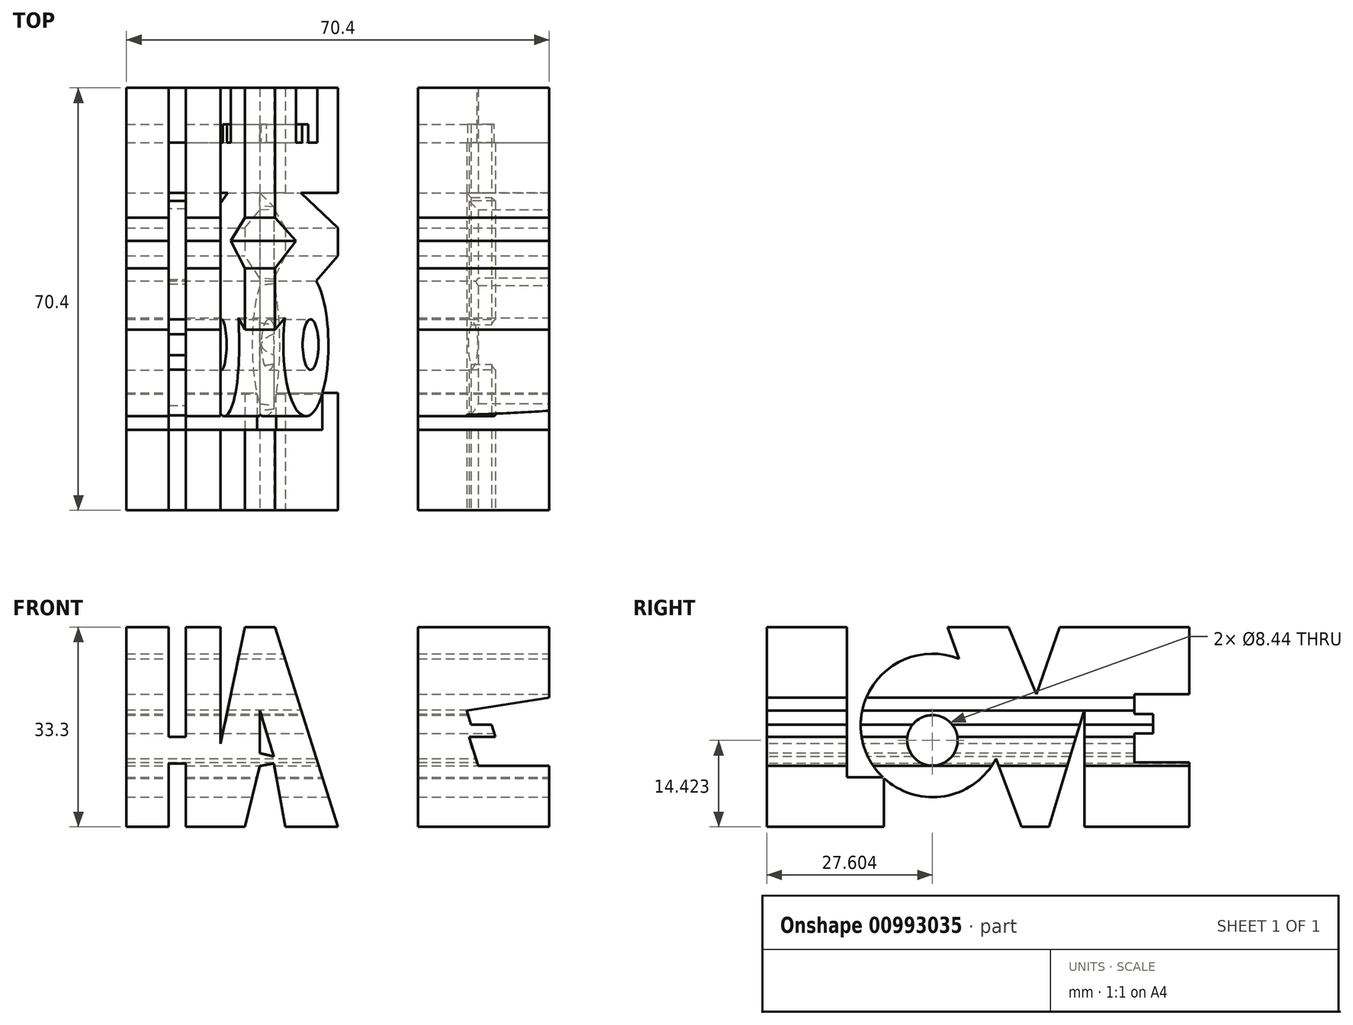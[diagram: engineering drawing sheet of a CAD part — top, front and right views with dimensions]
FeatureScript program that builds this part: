
annotation { "Feature Type Name" : "Feature", "Feature Type Description" : "" }
export const myFeature = defineFeature(function(context is Context, id is Id, definition is map)
    precondition{}
    {
        {
            var Q0;
            Q0=qCreatedBy(makeId("Top.planeOp"),FACE);
            var sketch = newSketch(context, id + "F0", { "sketchPlane" : qUnion([Q0])});
            skLineSegment(sketch, "E0.bottom", {"start": v(35.2, 35.2) * mm, "end": v(-35.2, 35.2) * mm});
            skLineSegment(sketch, "E0.top", {"start": v(35.2, -35.2) * mm, "end": v(-35.2, -35.2) * mm});
            skLineSegment(sketch, "E0.left", {"start": v(35.2, 35.2) * mm, "end": v(35.2, -35.2) * mm});
            skLineSegment(sketch, "E0.right", {"start": v(-35.2, 35.2) * mm, "end": v(-35.2, -35.2) * mm});
            skPoint(sketch, "E0.middle", {"position": v(0, 0) * mm});
            skSolve(sketch);
        }
        {
            var Q0;
            Q0=makeQuery(id+"F0.imprint","IMPRINT",FACE,{"disambiguationData":[TD([[makeQuery(id+"F0.imprint","IMPRINT",EDGE,{"derivedFrom":sQuery(id+"F0.wireOp",EDGE,"E0.bottom")}),1.0]])]});
            extrude(context, id + "F1", {"entities" : qUnion([Q0]), "depth" : 33.3 * mm, "offsetDistance" : 25 * mm});
        }
        {
            var Q0;
            Q0=makeQuery(id+"F1.opExtrude","SWEPT_FACE",FACE,{"disambiguationData":[OSD([sQuery(id+"F0.wireOp",EDGE,"E0.left")])]});
            var sketch = newSketch(context, id + "F2", { "sketchPlane" : qUnion([Q0])});
            skLineSegment(sketch, "E1", {"start": v(-35.2, 33.3) * mm, "end": v(-35.2, 0) * mm});
            skLineSegment(sketch, "E2", {"start": v(-35.2, 0) * mm, "end": v(-15.67, 0) * mm});
            skLineSegment(sketch, "E3", {"start": v(-15.67, 0) * mm, "end": v(-15.67, 8.27) * mm});
            skLineSegment(sketch, "E4", {"start": v(-15.67, 8.27) * mm, "end": v(-21.83, 8.27) * mm});
            skLineSegment(sketch, "E5", {"start": v(-21.83, 8.27) * mm, "end": v(-21.83, 33.3) * mm});
            skLineSegment(sketch, "E6", {"start": v(-21.83, 33.3) * mm, "end": v(-35.2, 33.3) * mm});
            skCircle(sketch, "E7", {"center": v(-7.6, 14.42) * mm, "radius": 4.22 * mm});
            skCircle(sketch, "E8", {"center": v(-7.6, 16.92) * mm, "radius": 11.96 * mm});
            skLineSegment(sketch, "E9", {"start": v(-5.1, 33.3) * mm, "end": v(7.21, 0) * mm});
            skLineSegment(sketch, "E10", {"start": v(7.21, 0) * mm, "end": v(11.83, 0) * mm});
            skLineSegment(sketch, "E11", {"start": v(11.83, 0) * mm, "end": v(21.83, 33.3) * mm});
            skLineSegment(sketch, "E12", {"start": v(21.83, 33.3) * mm, "end": v(13.56, 33.3) * mm});
            skLineSegment(sketch, "E13", {"start": v(13.56, 33.3) * mm, "end": v(9.71, 22.12) * mm});
            skLineSegment(sketch, "E14", {"start": v(9.71, 22.12) * mm, "end": v(5.1, 33.3) * mm});
            skLineSegment(sketch, "E15", {"start": v(5.1, 33.3) * mm, "end": v(-5.1, 33.3) * mm});
            skLineSegment(sketch, "E16", {"start": v(17.7, 33.3) * mm, "end": v(17.7, 0) * mm});
            skLineSegment(sketch, "E17", {"start": v(17.7, 0) * mm, "end": v(35.2, 0) * mm});
            skLineSegment(sketch, "E18", {"start": v(35.2, 0) * mm, "end": v(35.2, 10.77) * mm});
            skLineSegment(sketch, "E19", {"start": v(35.2, 10.77) * mm, "end": v(26.06, 10.77) * mm});
            skLineSegment(sketch, "E20", {"start": v(26.06, 10.77) * mm, "end": v(26.06, 15.58) * mm});
            skLineSegment(sketch, "E21", {"start": v(17.7, 33.3) * mm, "end": v(35.2, 33.3) * mm});
            skLineSegment(sketch, "E22", {"start": v(35.2, 33.3) * mm, "end": v(35.2, 22.12) * mm});
            skLineSegment(sketch, "E23", {"start": v(35.2, 22.12) * mm, "end": v(26.06, 22.12) * mm});
            skLineSegment(sketch, "E24", {"start": v(26.06, 22.12) * mm, "end": v(26.06, 18.85) * mm});
            skLineSegment(sketch, "E25", {"start": v(26.06, 18.85) * mm, "end": v(29.13, 18.85) * mm});
            skLineSegment(sketch, "E26", {"start": v(29.13, 18.85) * mm, "end": v(29.13, 15.58) * mm});
            skLineSegment(sketch, "E27", {"start": v(29.13, 15.58) * mm, "end": v(26.06, 15.58) * mm});
            skSolve(sketch);
        }
        {
            var Q0;
            Q0=makeQuery(id+"F2.imprint","IMPRINT",FACE,{"disambiguationData":[TD([[makeQuery(id+"F2.imprint","IMPRINT",EDGE,{"derivedFrom":sQuery(id+"F2.wireOp",EDGE,"E1")}),1.0]])]});
            var Q1;
            Q1=makeQuery(id+"F2.imprint","IMPRINT",FACE,{"disambiguationData":[TD([[makeQuery(id+"F2.imprint","IMPRINT",EDGE,{"derivedFrom":sQuery(id+"F2.wireOp",EDGE,"E7")}),-1.0]])]});
            var Q2;
            {var subQ0=sQuery(id+"F2.wireOp",EDGE,"E10");Q2=makeQuery(id+"F2.imprint","IMPRINT",FACE,{"disambiguationData":[TD([[makeQuery(id+"F2.imprint","IMPRINT",EDGE,{"derivedFrom":subQ0}),-1.0]])]});}
            var Q3;
            {var subQ0=sQuery(id+"F2.wireOp",EDGE,"E21");var subQ1=sQuery(id+"F2.wireOp",EDGE,"E11");var subQ2=makeQuery(id+"F2.imprint","INTERSECT",VERTEX,{"derivedFrom":[subQ1,subQ0]});Q3=makeQuery(id+"F2.imprint","IMPRINT",FACE,{"disambiguationData":[TD([[makeQuery(id+"F2.imprint","IMPRINT",EDGE,{"disambiguationData":[TD([[subQ2,1.0]])],"derivedFrom":subQ1}),1.0]])]});}
            var Q4;
            {var subQ6=sQuery(id+"F2.wireOp",EDGE,"E17");Q4=makeQuery(id+"F2.imprint","IMPRINT",FACE,{"disambiguationData":[TD([[makeQuery(id+"F2.imprint","IMPRINT",EDGE,{"derivedFrom":subQ6}),-1.0]])]});}
            var Q5;
            {var subQ0=sQuery(id+"F2.wireOp",EDGE,"E9");var subQ1=sQuery(id+"F2.wireOp",EDGE,"E8");var subQ2=makeQuery(id+"F2.imprint","INTERSECT",VERTEX,{"disambiguationData":[OD(0.0)],"derivedFrom":[subQ1,subQ0]});Q5=makeQuery(id+"F2.imprint","IMPRINT",FACE,{"disambiguationData":[TD([[makeQuery(id+"F2.imprint","IMPRINT",EDGE,{"disambiguationData":[TD([[subQ2,1.0]])],"derivedFrom":subQ1}),1.0]])]});}
            var Q6;
            {var subQ0=sQuery(id+"F2.wireOp",EDGE,"E4");var subQ1=sQuery(id+"F2.wireOp",EDGE,"E3");var subQ2=makeQuery(id+"F2.imprint","INTERSECT",VERTEX,{"derivedFrom":[subQ1,subQ0]});Q6=makeQuery(id+"F2.imprint","IMPRINT",FACE,{"disambiguationData":[TD([[makeQuery(id+"F2.imprint","IMPRINT",EDGE,{"disambiguationData":[TD([[subQ2,1.0]])],"derivedFrom":subQ1}),1.0]])]});}
            extrude(context, id + "F3", {"entities" : qUnion([Q0, Q1, Q2, Q3, Q4, Q5, Q6]), "operationType" : NewBodyOperationType.INTERSECT, "oppositeDirection" : true, "depth" : 88.7 * mm, "offsetDistance" : 25 * mm});
        }
        {
            var Q0;
            Q0=makeQuery(id+"F1.opExtrude","SWEPT_FACE",FACE,{"disambiguationData":[OSD([sQuery(id+"F0.wireOp",EDGE,"E0.top")])]});
            var sketch = newSketch(context, id + "F4", { "sketchPlane" : qUnion([Q0])});
            skLineSegment(sketch, "E28", {"start": v(-35.2, 33.3) * mm, "end": v(-35.2, 0) * mm});
            skLineSegment(sketch, "E29", {"start": v(-35.2, 0) * mm, "end": v(-28.17, 0) * mm});
            skLineSegment(sketch, "E30", {"start": v(-28.17, 0) * mm, "end": v(-28.17, 10.58) * mm});
            skLineSegment(sketch, "E31", {"start": v(-28.17, 10.58) * mm, "end": v(-25.29, 10.58) * mm});
            skLineSegment(sketch, "E32", {"start": v(-25.29, 10.58) * mm, "end": v(-25.29, 0) * mm});
            skLineSegment(sketch, "E33", {"start": v(-25.29, 0) * mm, "end": v(-19.52, 0) * mm});
            skLineSegment(sketch, "E34", {"start": v(-19.52, 0) * mm, "end": v(-19.52, 33.3) * mm});
            skLineSegment(sketch, "E35", {"start": v(-19.52, 33.3) * mm, "end": v(-25.29, 33.3) * mm});
            skLineSegment(sketch, "E36", {"start": v(-25.29, 33.3) * mm, "end": v(-25.29, 15) * mm});
            skLineSegment(sketch, "E37", {"start": v(-25.29, 15) * mm, "end": v(-28.17, 15) * mm});
            skLineSegment(sketch, "E38", {"start": v(-28.17, 15) * mm, "end": v(-28.17, 33.3) * mm});
            skLineSegment(sketch, "E39", {"start": v(-28.17, 33.3) * mm, "end": v(-35.2, 33.3) * mm});
            skLineSegment(sketch, "E40", {"start": v(-22.4, 0) * mm, "end": v(-15.48, 33.3) * mm});
            skLineSegment(sketch, "E41", {"start": v(-15.48, 33.3) * mm, "end": v(-10.48, 33.3) * mm});
            skLineSegment(sketch, "E42", {"start": v(-10.48, 33.3) * mm, "end": v(0, 0) * mm});
            skLineSegment(sketch, "E43", {"start": v(0, 0) * mm, "end": v(-8.75, 0) * mm});
            skLineSegment(sketch, "E44", {"start": v(-8.75, 0) * mm, "end": v(-10.67, 10.58) * mm});
            skLineSegment(sketch, "E45", {"start": v(-10.67, 10.58) * mm, "end": v(-12.97, 10.16) * mm});
            skLineSegment(sketch, "E46", {"start": v(-12.97, 10.16) * mm, "end": v(-15.48, 0) * mm});
            skLineSegment(sketch, "E47", {"start": v(-15.48, 0) * mm, "end": v(-22.4, 0) * mm});
            skLineSegment(sketch, "E48", {"start": v(-12.97, 12.3) * mm, "end": v(-10.67, 11.74) * mm});
            skLineSegment(sketch, "E49", {"start": v(-10.67, 11.74) * mm, "end": v(-12.97, 19.42) * mm});
            skLineSegment(sketch, "E50", {"start": v(-12.97, 19.42) * mm, "end": v(-12.97, 12.3) * mm});
            skLineSegment(sketch, "E51", {"start": v(-2.21, 0) * mm, "end": v(-2.21, 24.04) * mm});
            skLineSegment(sketch, "E52", {"start": v(-2.21, 24.04) * mm, "end": v(-10.67, 24.04) * mm});
            skLineSegment(sketch, "E53", {"start": v(-10.67, 24.04) * mm, "end": v(-10.48, 33.3) * mm});
            skLineSegment(sketch, "E54", {"start": v(-10.48, 33.3) * mm, "end": v(16.44, 33.3) * mm});
            skLineSegment(sketch, "E55", {"start": v(16.44, 33.3) * mm, "end": v(16.44, 24.04) * mm});
            skLineSegment(sketch, "E56", {"start": v(16.44, 24.04) * mm, "end": v(5.87, 24.04) * mm});
            skLineSegment(sketch, "E57", {"start": v(5.87, 24.04) * mm, "end": v(5.87, 0) * mm});
            skLineSegment(sketch, "E58", {"start": v(5.87, 0) * mm, "end": v(-2.21, 0) * mm});
            skLineSegment(sketch, "E59", {"start": v(13.37, 33.3) * mm, "end": v(13.37, 0) * mm});
            skLineSegment(sketch, "E60", {"start": v(13.37, 0) * mm, "end": v(35.2, 0) * mm});
            skLineSegment(sketch, "E61", {"start": v(35.2, 0) * mm, "end": v(35.2, 10.16) * mm});
            skLineSegment(sketch, "E62", {"start": v(35.2, 10.16) * mm, "end": v(23.37, 10.16) * mm});
            skLineSegment(sketch, "E63", {"start": v(23.37, 10.16) * mm, "end": v(21.84, 15) * mm});
            skLineSegment(sketch, "E64", {"start": v(21.84, 15) * mm, "end": v(26.25, 15) * mm});
            skLineSegment(sketch, "E65", {"start": v(26.25, 15) * mm, "end": v(25.6, 17.04) * mm});
            skLineSegment(sketch, "E66", {"start": v(25.6, 17.04) * mm, "end": v(22.21, 17.04) * mm});
            skLineSegment(sketch, "E67", {"start": v(22.21, 17.04) * mm, "end": v(21.46, 19.42) * mm});
            skLineSegment(sketch, "E68", {"start": v(21.46, 19.42) * mm, "end": v(35.2, 21.54) * mm});
            skLineSegment(sketch, "E69", {"start": v(35.2, 21.54) * mm, "end": v(35.2, 33.3) * mm});
            skLineSegment(sketch, "E70", {"start": v(35.2, 33.3) * mm, "end": v(13.37, 33.3) * mm});
            skSolve(sketch);
        }
        {
            var Q0;
            Q0=makeQuery(id+"F4.imprint","IMPRINT",FACE,{"disambiguationData":[TD([[makeQuery(id+"F4.imprint","IMPRINT",EDGE,{"derivedFrom":sQuery(id+"F4.wireOp",EDGE,"E28")}),1.0]])]});
            var Q1;
            {var subQ0=sQuery(id+"F4.wireOp",EDGE,"E47");var subQ1=sQuery(id+"F4.wireOp",EDGE,"E34");var subQ2=makeQuery(id+"F4.imprint","INTERSECT",VERTEX,{"derivedFrom":[subQ1,subQ0]});Q1=makeQuery(id+"F4.imprint","IMPRINT",FACE,{"disambiguationData":[TD([[makeQuery(id+"F4.imprint","IMPRINT",EDGE,{"disambiguationData":[TD([[subQ2,-1.0]])],"derivedFrom":subQ1}),1.0]])]});}
            var Q2;
            {var subQ6=sQuery(id+"F4.wireOp",EDGE,"E41");Q2=makeQuery(id+"F4.imprint","IMPRINT",FACE,{"disambiguationData":[TD([[makeQuery(id+"F4.imprint","IMPRINT",EDGE,{"derivedFrom":subQ6}),1.0]])]});}
            var Q3;
            {var subQ0=sQuery(id+"F4.wireOp",EDGE,"E58");var subQ1=sQuery(id+"F4.wireOp",EDGE,"E42");var subQ2=makeQuery(id+"F4.imprint","INTERSECT",VERTEX,{"derivedFrom":[subQ1,subQ0]});Q3=makeQuery(id+"F4.imprint","IMPRINT",FACE,{"disambiguationData":[TD([[makeQuery(id+"F4.imprint","IMPRINT",EDGE,{"disambiguationData":[TD([[subQ2,1.0]])],"derivedFrom":subQ1}),-1.0]])]});}
            var Q4;
            {var subQ9=sQuery(id+"F4.wireOp",EDGE,"E54");Q4=makeQuery(id+"F4.imprint","IMPRINT",FACE,{"disambiguationData":[TD([[makeQuery(id+"F4.imprint","IMPRINT",EDGE,{"derivedFrom":subQ9}),1.0]])]});}
            var Q5;
            {var subQ0=sQuery(id+"F4.wireOp",EDGE,"E53");Q5=makeQuery(id+"F4.imprint","IMPRINT",FACE,{"disambiguationData":[TD([[makeQuery(id+"F4.imprint","IMPRINT",EDGE,{"derivedFrom":subQ0}),-1.0]])]});}
            var Q6;
            {var subQ0=sQuery(id+"F4.wireOp",EDGE,"E55");Q6=makeQuery(id+"F4.imprint","IMPRINT",FACE,{"disambiguationData":[TD([[makeQuery(id+"F4.imprint","IMPRINT",EDGE,{"derivedFrom":subQ0}),-1.0]])]});}
            var Q7;
            {var subQ0=sQuery(id+"F4.wireOp",EDGE,"E55");Q7=makeQuery(id+"F4.imprint","IMPRINT",FACE,{"disambiguationData":[TD([[makeQuery(id+"F4.imprint","IMPRINT",EDGE,{"derivedFrom":subQ0}),1.0]])]});}
            extrude(context, id + "F5", {"entities" : qUnion([Q0, Q1, Q2, Q3, Q4, Q5, Q6, Q7]), "operationType" : NewBodyOperationType.INTERSECT, "oppositeDirection" : true, "depth" : 88 * mm, "offsetDistance" : 25 * mm});
        }
    });
